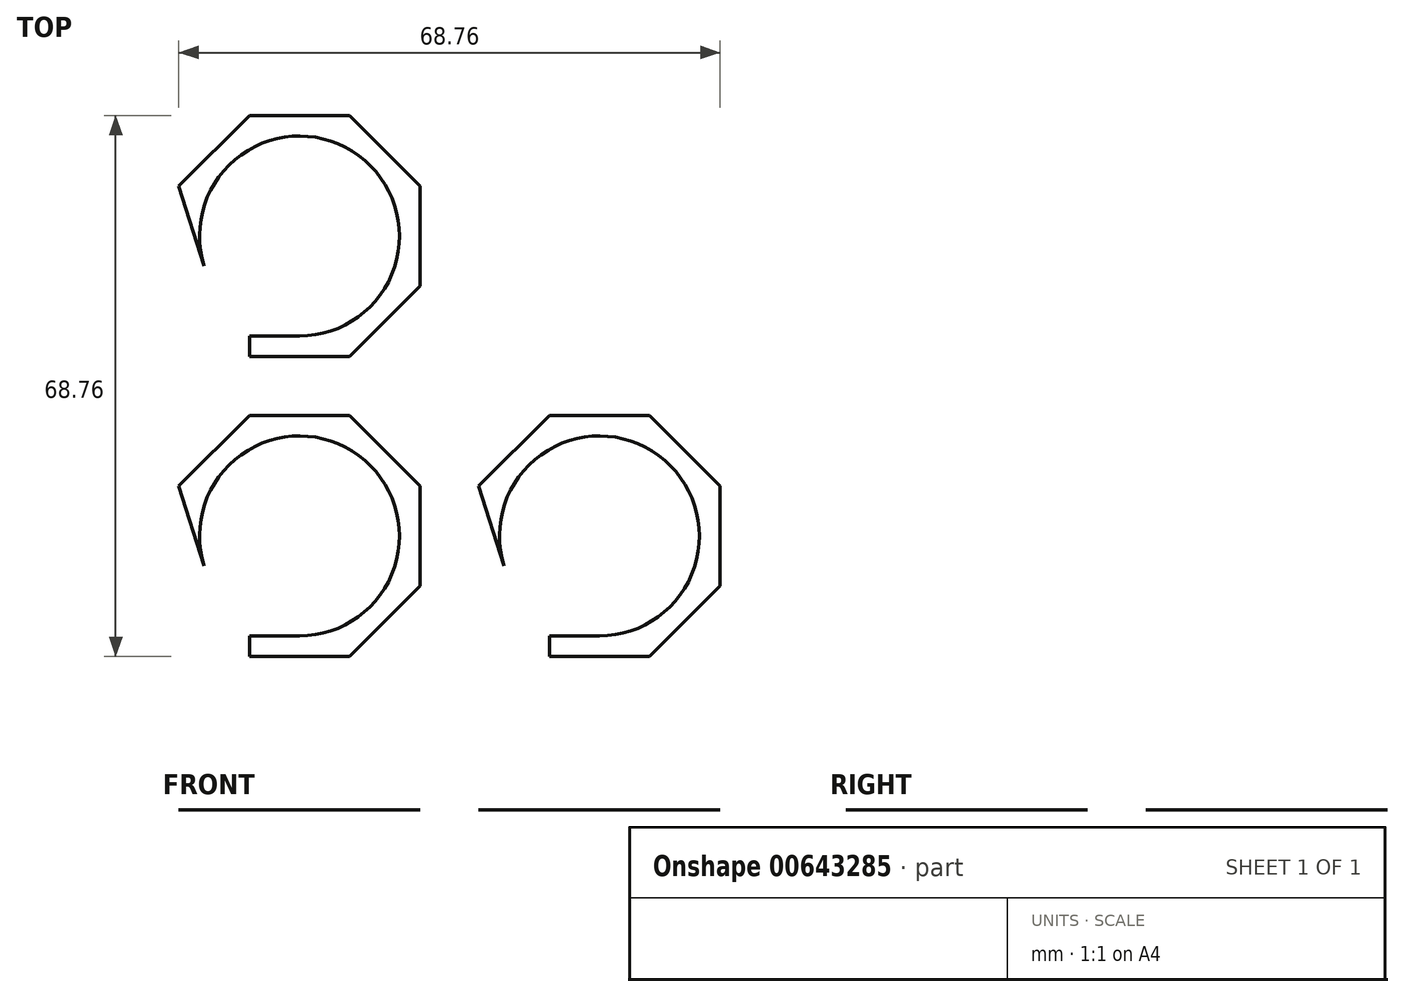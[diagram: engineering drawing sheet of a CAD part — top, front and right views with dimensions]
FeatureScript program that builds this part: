
annotation { "Feature Type Name" : "Feature", "Feature Type Description" : "" }
export const myFeature = defineFeature(function(context is Context, id is Id, definition is map)
    precondition{}
    {
        {
            var Q0;
            Q0=qCreatedBy(makeId("Top.planeOp"),FACE);
            var sketch = newSketch(context, id + "F0", { "sketchPlane" : qUnion([Q0])});
            skLineSegment(sketch, "E0", {"start": v(0, 0) * mm, "end": v(12.7, 0) * mm});
            skLineSegment(sketch, "E1", {"start": v(15.24, 2.54) * mm, "end": v(12.7, 0) * mm});
            skLineSegment(sketch, "E2", {"start": v(12.7, 0) * mm, "end": v(21.68, 8.98) * mm});
            skLineSegment(sketch, "E3", {"start": v(21.68, 8.98) * mm, "end": v(21.68, 21.68) * mm});
            skLineSegment(sketch, "E4", {"start": v(19.14, 24.22) * mm, "end": v(21.68, 21.68) * mm});
            skLineSegment(sketch, "E5", {"start": v(21.68, 21.68) * mm, "end": v(12.7, 30.66) * mm});
            skLineSegment(sketch, "E6", {"start": v(12.7, 30.66) * mm, "end": v(0, 30.66) * mm});
            skLineSegment(sketch, "E7", {"start": v(-2.54, 28.12) * mm, "end": v(0, 30.66) * mm});
            skLineSegment(sketch, "E8", {"start": v(0, 30.66) * mm, "end": v(-8.98, 21.68) * mm});
            skPoint(sketch, "E9.center.orphan", {"position": v(6.35, 15.33) * mm});
            skCircle(sketch, "E10", {"center": v(6.35, 15.33) * mm, "radius": 12.7 * mm});
            skLineSegment(sketch, "E11", {"start": v(-8.98, 21.68) * mm, "end": v(-5.76, 11.5) * mm});
            skLineSegment(sketch, "E12", {"start": v(6.35, 2.63) * mm, "end": v(2.39, 2.63) * mm});
            skPoint(sketch, "E13.end.orphan", {"position": v(2.39, 2.63) * mm});
            skPoint(sketch, "E14.orphan", {"position": v(-1.58, 2.63) * mm});
            skLineSegment(sketch, "E15", {"start": v(0, 0) * mm, "end": v(0, 2.63) * mm});
            skLineSegment(sketch, "E16", {"start": v(2.39, 2.63) * mm, "end": v(0, 2.63) * mm});
            skSolve(sketch);
        }
        {
            var Q0;
            {var subQ5=sQuery(id+"F0.wireOp",EDGE,"E0");Q0=makeQuery(id+"F0.imprint","IMPRINT",FACE,{"disambiguationData":[TD([[makeQuery(id+"F0.imprint","IMPRINT",EDGE,{"derivedFrom":subQ5}),1.0]])]});}
            extrude(context, id + "F1", {"entities" : qUnion([Q0]), "depth" : 1 / 203.2 * mm, "offsetDistance" : 25.4 * mm});
        }
        {
            var Q0;
            Q0=makeQuery(id+"F1.opExtrude","SWEPT_BODY",BODY,{"disambiguationData":[OSD([sQuery(id+"F0.wireOp",EDGE,"E0"),sQuery(id+"F0.wireOp",EDGE,"E2"),sQuery(id+"F0.wireOp",EDGE,"E3"),sQuery(id+"F0.wireOp",EDGE,"E5"),sQuery(id+"F0.wireOp",EDGE,"E6"),sQuery(id+"F0.wireOp",EDGE,"E8"),sQuery(id+"F0.wireOp",EDGE,"E10"),sQuery(id+"F0.wireOp",EDGE,"E11"),sQuery(id+"F0.wireOp",EDGE,"E12"),sQuery(id+"F0.wireOp",EDGE,"E15"),sQuery(id+"F0.wireOp",EDGE,"E16")])]});
            transform(context, id + "F2", {"entities" : qUnion([Q0]), "transformType" : TransformType.TRANSLATION_3D, "dx" : 0 * mm, "dy" : 38.1 * mm, "dz" : 0 * mm, "makeCopy" : true});
        }
        {
            var Q0;
            Q0=makeQuery(id+"F1.opExtrude","SWEPT_BODY",BODY,{"disambiguationData":[OSD([sQuery(id+"F0.wireOp",EDGE,"E0"),sQuery(id+"F0.wireOp",EDGE,"E2"),sQuery(id+"F0.wireOp",EDGE,"E3"),sQuery(id+"F0.wireOp",EDGE,"E5"),sQuery(id+"F0.wireOp",EDGE,"E6"),sQuery(id+"F0.wireOp",EDGE,"E8"),sQuery(id+"F0.wireOp",EDGE,"E10"),sQuery(id+"F0.wireOp",EDGE,"E11"),sQuery(id+"F0.wireOp",EDGE,"E12"),sQuery(id+"F0.wireOp",EDGE,"E15"),sQuery(id+"F0.wireOp",EDGE,"E16")])]});
            transform(context, id + "F3", {"entities" : qUnion([Q0]), "transformType" : TransformType.TRANSLATION_3D, "dx" : 38.1 * mm, "dy" : 0 * mm, "dz" : 0 * mm, "makeCopy" : true});
        }
    });
